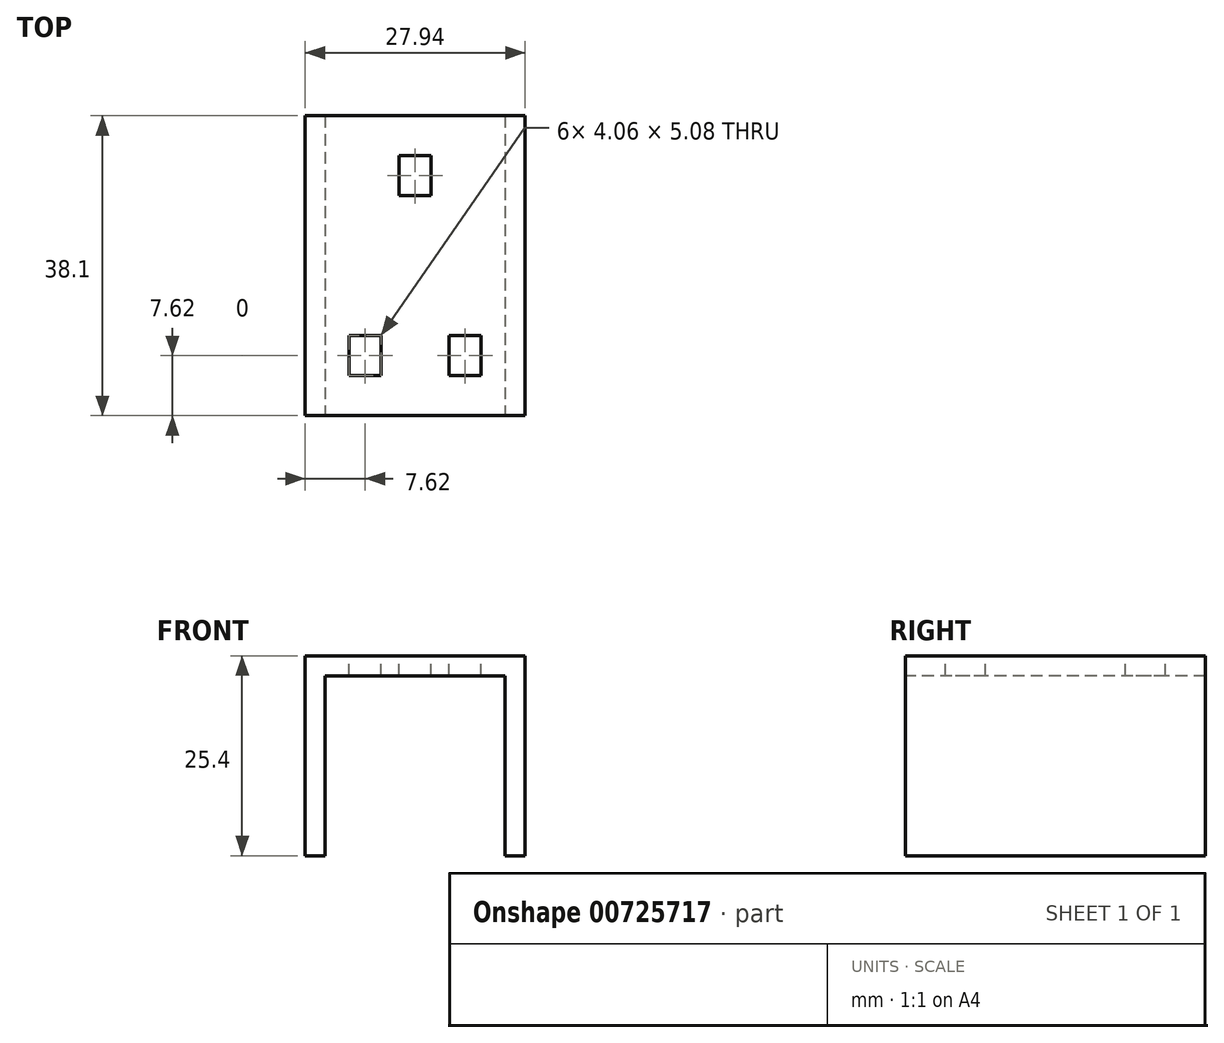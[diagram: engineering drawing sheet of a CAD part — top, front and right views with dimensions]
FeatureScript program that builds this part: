
annotation { "Feature Type Name" : "Feature", "Feature Type Description" : "" }
export const myFeature = defineFeature(function(context is Context, id is Id, definition is map)
    precondition{}
    {
        {
            var Q0;
            Q0=qCreatedBy(makeId("Top.planeOp"),FACE);
            var sketch = newSketch(context, id + "F0", { "sketchPlane" : qUnion([Q0])});
            skLineSegment(sketch, "E0.bottom", {"start": v(13.97, 19.05) * mm, "end": v(-13.97, 19.05) * mm});
            skLineSegment(sketch, "E0.top", {"start": v(13.97, -19.05) * mm, "end": v(-13.97, -19.05) * mm});
            skLineSegment(sketch, "E0.left", {"start": v(13.97, 19.05) * mm, "end": v(13.97, -19.05) * mm});
            skLineSegment(sketch, "E0.right", {"start": v(-13.97, 19.05) * mm, "end": v(-13.97, -19.05) * mm});
            skPoint(sketch, "E0.middle", {"position": v(0, 0) * mm});
            skSolve(sketch);
        }
        {
            var Q0;
            Q0 = qSketchRegion(id + "F0", true);
            extrude(context, id + "F1", {"entities" : qUnion([Q0]), "depth" : 25.4 * mm, "offsetDistance" : 25.4 * mm});
        }
        {
            var Q0;
            Q0=makeQuery(id+"F1.opExtrude","CAP_FACE",FACE,{"disambiguationData":[OSD([sQuery(id+"F0.wireOp",EDGE,"E0.bottom"),sQuery(id+"F0.wireOp",EDGE,"E0.top"),sQuery(id+"F0.wireOp",EDGE,"E0.left"),sQuery(id+"F0.wireOp",EDGE,"E0.right")])],"isStart":false});
            var sketch = newSketch(context, id + "F2", { "sketchPlane" : qUnion([Q0])});
            skLineSegment(sketch, "E1.bottom", {"start": v(2.03, 13.97) * mm, "end": v(-2.03, 13.97) * mm});
            skLineSegment(sketch, "E1.top", {"start": v(2.03, 8.9) * mm, "end": v(-2.03, 8.9) * mm});
            skLineSegment(sketch, "E1.left", {"start": v(2.03, 13.97) * mm, "end": v(2.03, 8.9) * mm});
            skLineSegment(sketch, "E1.right", {"start": v(-2.03, 13.97) * mm, "end": v(-2.03, 8.9) * mm});
            skPoint(sketch, "E1.middle", {"position": v(0, 11.43) * mm});
            skLineSegment(sketch, "E2.bottom", {"start": v(-4.32, -8.89) * mm, "end": v(-8.38, -8.89) * mm});
            skLineSegment(sketch, "E2.top", {"start": v(-4.32, -13.97) * mm, "end": v(-8.38, -13.97) * mm});
            skLineSegment(sketch, "E2.left", {"start": v(-4.32, -8.89) * mm, "end": v(-4.32, -13.97) * mm});
            skLineSegment(sketch, "E2.right", {"start": v(-8.38, -8.89) * mm, "end": v(-8.38, -13.97) * mm});
            skPoint(sketch, "E2.middle", {"position": v(-6.35, -11.43) * mm});
            skLineSegment(sketch, "E3.bottom", {"start": v(8.38, -8.9) * mm, "end": v(4.32, -8.9) * mm});
            skLineSegment(sketch, "E3.top", {"start": v(8.38, -13.97) * mm, "end": v(4.32, -13.97) * mm});
            skLineSegment(sketch, "E3.left", {"start": v(8.38, -8.89) * mm, "end": v(8.38, -13.97) * mm});
            skLineSegment(sketch, "E3.right", {"start": v(4.32, -8.89) * mm, "end": v(4.32, -13.97) * mm});
            skPoint(sketch, "E3.middle", {"position": v(6.35, -11.43) * mm});
            skSolve(sketch);
        }
        {
            var Q0;
            Q0=makeQuery(id+"F1.opExtrude","SWEPT_FACE",FACE,{"disambiguationData":[OSD([sQuery(id+"F0.wireOp",EDGE,"E0.top")])]});
            var Q1;
            Q1=makeQuery(id+"F1.opExtrude","CAP_FACE",FACE,{"disambiguationData":[OSD([sQuery(id+"F0.wireOp",EDGE,"E0.bottom"),sQuery(id+"F0.wireOp",EDGE,"E0.top"),sQuery(id+"F0.wireOp",EDGE,"E0.left"),sQuery(id+"F0.wireOp",EDGE,"E0.right")])],"isStart":true});
            var Q2;
            Q2=makeQuery(id+"F1.opExtrude","SWEPT_FACE",FACE,{"disambiguationData":[OSD([sQuery(id+"F0.wireOp",EDGE,"E0.bottom")])]});
            shell(context, id + "F3", {"entities" : qUnion([Q0, Q1, Q2]), "thickness" : 2.54 * mm});
        }
        {
            var Q0;
            Q0 = qSketchRegion(id + "F2", true);
            extrude(context, id + "F4", {"entities" : qUnion([Q0]), "operationType" : NewBodyOperationType.REMOVE, "oppositeDirection" : true, "depth" : 25.4 * mm, "offsetDistance" : 25.4 * mm});
        }
    });
